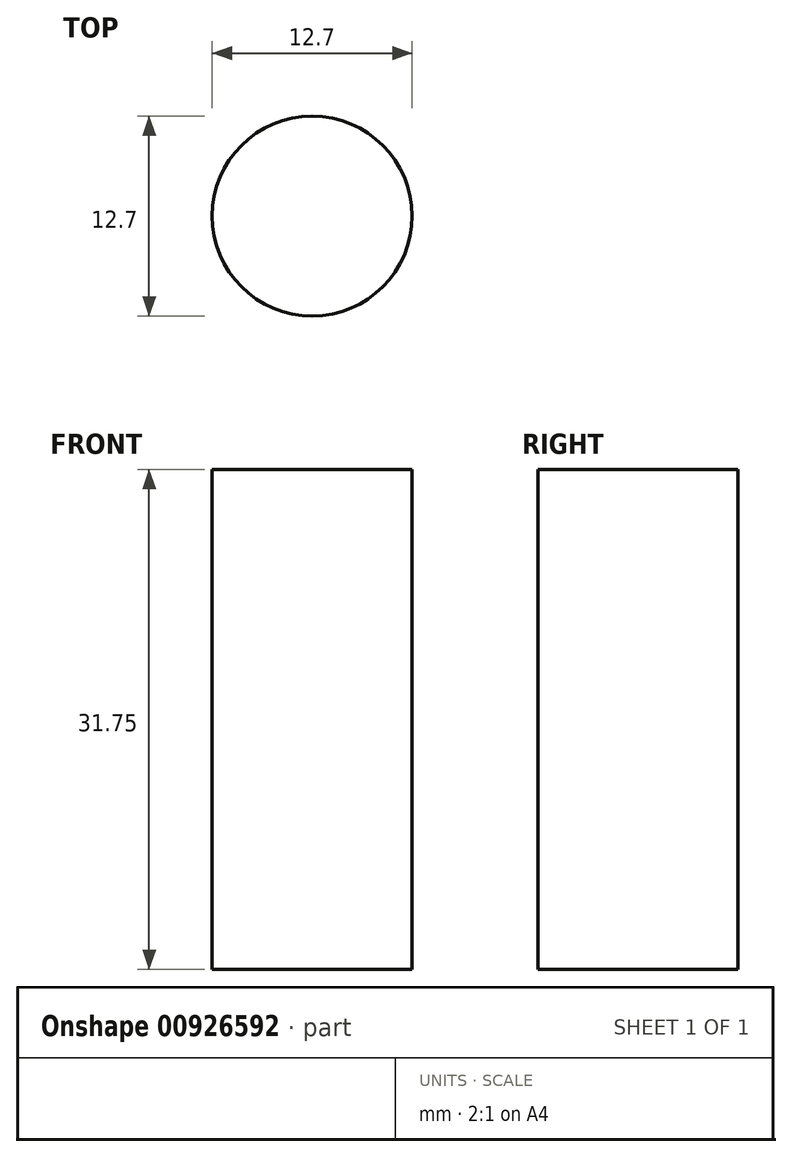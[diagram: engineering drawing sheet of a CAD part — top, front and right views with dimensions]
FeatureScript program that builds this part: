
annotation { "Feature Type Name" : "Feature", "Feature Type Description" : "" }
export const myFeature = defineFeature(function(context is Context, id is Id, definition is map)
    precondition{}
    {
        {
            var Q0;
            Q0=qCreatedBy(makeId("Top.planeOp"),FACE);
            var sketch = newSketch(context, id + "F0", { "sketchPlane" : qUnion([Q0])});
            skCircle(sketch, "E0", {"center": v(0, 0) * mm, "radius": 6.35 * mm});
            skSolve(sketch);
        }
        {
            var Q0;
            Q0=makeQuery(id+"F0.imprint","IMPRINT",FACE,{"disambiguationData":[TD([[makeQuery(id+"F0.imprint","IMPRINT",EDGE,{"derivedFrom":sQuery(id+"F0.wireOp",EDGE,"E0")}),1.0]])]});
            extrude(context, id + "F1", {"entities" : qUnion([Q0]), "depth" : 31.75 * mm, "offsetDistance" : 25.4 * mm});
        }
    });
